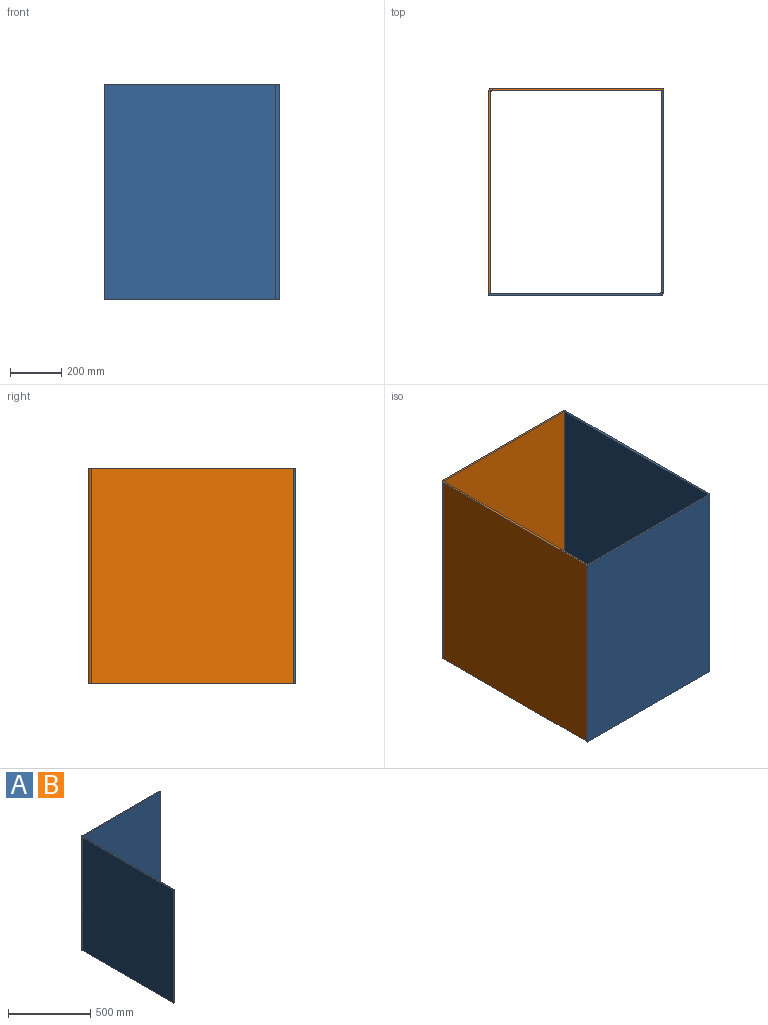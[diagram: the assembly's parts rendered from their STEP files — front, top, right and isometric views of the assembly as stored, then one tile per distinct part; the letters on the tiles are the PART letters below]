
ASSEMBLY  parts=2 mates=1
PART A: 14 faces, bbox 680x800x840 mm
  f0: plane 787x8mm, normal (0,0,-1), area 6296mm2, adj f2,f3,f4,f11
  f1: plane 787x8mm, normal (0,0,1), area 6296mm2, adj f2,f3,f4,f10
  f2: plane 840x8mm, normal (0,-1,0), area 6720mm2, adj f0,f1,f3,f4
  f3: plane 840x787mm, normal (1,0,0), area 661080mm2, adj f0,f1,f2,f13
  f4: plane 840x787mm, normal (-1,0,0), area 661080mm2, adj f0,f1,f2,f12
  f5: plane 667x8mm, normal (0,0,-1), area 5336mm2, adj f6,f8,f9,f11
  f6: plane 840x8mm, normal (1,0,0), area 6720mm2, adj f5,f7,f8,f9
  f7: plane 667x8mm, normal (0,0,1), area 5336mm2, adj f6,f8,f9,f10
  f8: plane 840x667mm, normal (0,-1,0), area 560280mm2, adj f5,f6,f7,f13
  f9: plane 840x667mm, normal (0,1,0), area 560280mm2, adj f5,f6,f7,f12
  f10: plane 13x13mm, normal (0,0,1), area 113.1mm2, adj f1,f7,f12,f13
  f11: plane 13x13mm, normal (0,0,-1), area 113.1mm2, adj f0,f5,f12,f13
  f12: cylinder r=13mm len=840mm, axis (0,0,1), area 17153.1mm2, adj f4,f9,f10,f11
  f13: cylinder r=5mm len=840mm, axis (0,0,1), area 6597.3mm2, adj f3,f8,f10,f11
PART B: same geometry as A
PLACE A rot(axis=(0,0,1),180deg) t=(-102.7,553.09,205.02)mm
PLACE B t=(-782.7,-238.91,205.02)mm
MATE fastened A.f8 <-> B.f2  axis (0,1,0) through (-782.7,-238.91,205.02)mm
